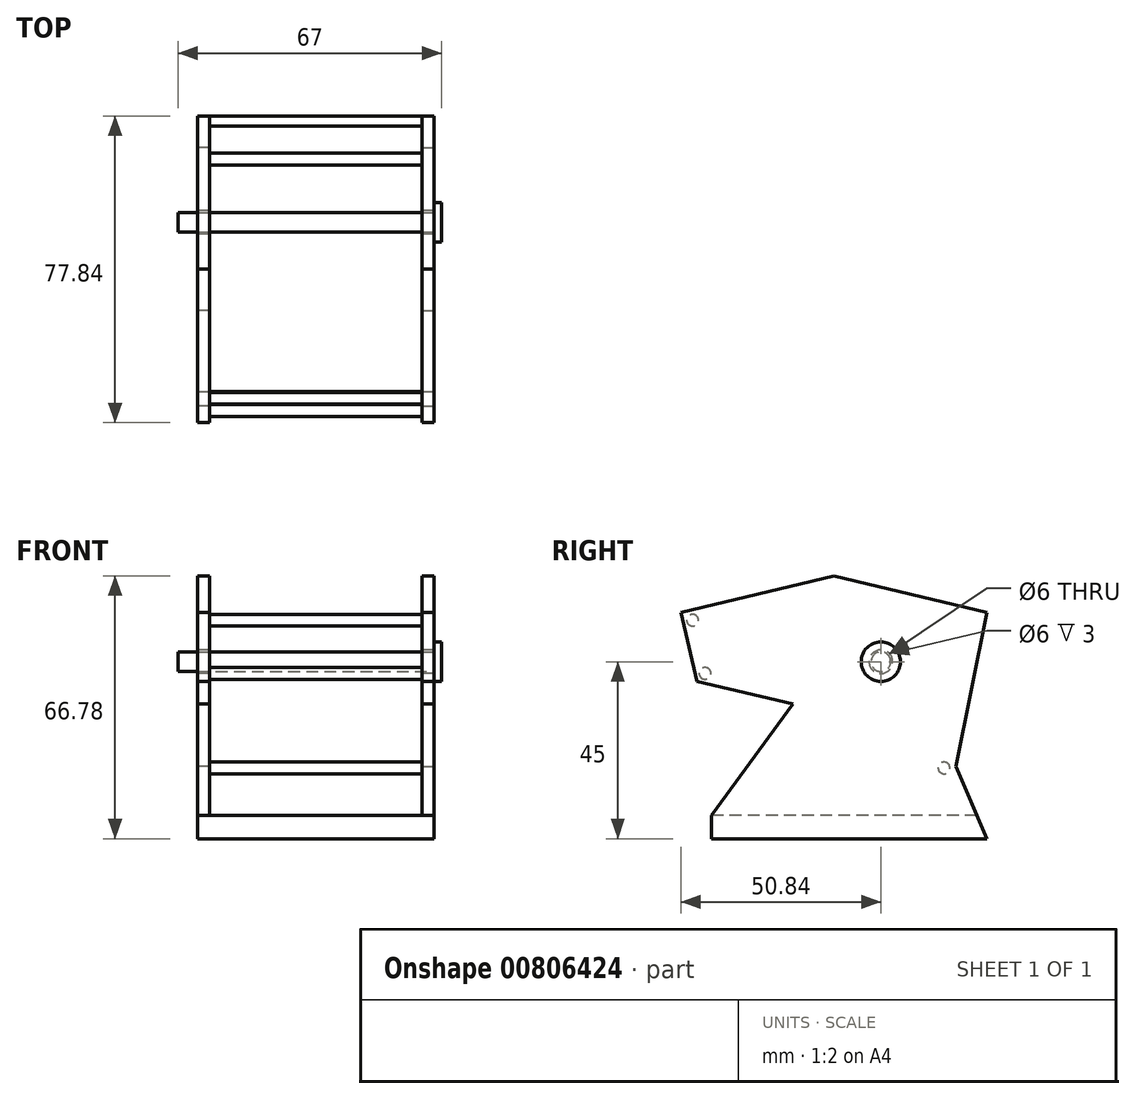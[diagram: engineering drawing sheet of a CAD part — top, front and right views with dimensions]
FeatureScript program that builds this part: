
annotation { "Feature Type Name" : "Feature", "Feature Type Description" : "" }
export const myFeature = defineFeature(function(context is Context, id is Id, definition is map)
    precondition{}
    {
        {
            var Q0;
            Q0=qCreatedBy(makeId("Right.planeOp"),FACE);
            var sketch = newSketch(context, id + "F0", { "sketchPlane" : qUnion([Q0])});
            skLineSegment(sketch, "E0", {"start": v(-35, 0) * mm, "end": v(35, 0) * mm});
            skLineSegment(sketch, "E1", {"start": v(35, 0) * mm, "end": v(27.05, 18.35) * mm});
            skLineSegment(sketch, "E2", {"start": v(27.05, 18.35) * mm, "end": v(35, 57.55) * mm});
            skLineSegment(sketch, "E3", {"start": v(35, 57.55) * mm, "end": v(-3.92, 66.78) * mm});
            skLineSegment(sketch, "E4", {"start": v(-3.92, 66.78) * mm, "end": v(-42.84, 57.55) * mm});
            skLineSegment(sketch, "E5", {"start": v(-42.84, 57.55) * mm, "end": v(-38.69, 40.04) * mm});
            skLineSegment(sketch, "E6", {"start": v(-38.69, 40.04) * mm, "end": v(-14.36, 34.27) * mm});
            skLineSegment(sketch, "E7", {"start": v(-14.36, 34.27) * mm, "end": v(-35, 6) * mm});
            skLineSegment(sketch, "E8", {"start": v(-35, 6) * mm, "end": v(-35, 0) * mm});
            skLineSegment(sketch, "E9", {"start": v(-35, 6) * mm, "end": v(32.4, 6) * mm});
            skSolve(sketch);
        }
        {
            var Q0;
            {var subQ0=sQuery(id+"F0.wireOp",EDGE,"E0");Q0=makeQuery(id+"F0.imprint","IMPRINT",FACE,{"disambiguationData":[TD([[makeQuery(id+"F0.imprint","IMPRINT",EDGE,{"derivedFrom":subQ0}),1.0]])]});}
            extrude(context, id + "F1", {"entities" : qUnion([Q0]), "oppositeDirection" : true, "depth" : 60 * mm, "offsetDistance" : 25 * mm});
        }
        {
            var Q0;
            {var subQ0=sQuery(id+"F0.wireOp",EDGE,"E2");Q0=makeQuery(id+"F0.imprint","IMPRINT",FACE,{"disambiguationData":[TD([[makeQuery(id+"F0.imprint","IMPRINT",EDGE,{"derivedFrom":subQ0}),1.0]])]});}
            extrude(context, id + "F2", {"entities" : qUnion([Q0]), "operationType" : NewBodyOperationType.ADD, "oppositeDirection" : true, "depth" : 3 * mm, "offsetDistance" : 25 * mm});
        }
        {
            var Q0;
            Q0=qCreatedBy(makeId("Right.planeOp"),FACE);
            cPlane(context, id + "F3", {"entities" : qUnion([Q0]), "cplaneType" : CPlaneType.OFFSET, "offset" : 60 * mm, "oppositeDirection" : true, "width" : 150 * mm, "height" : 150 * mm});
        }
        {
            var Q0;
            Q0=qCreatedBy(id+"F3.planeOp",FACE);
            var sketch = newSketch(context, id + "F4", { "sketchPlane" : qUnion([Q0])});
            skLineSegment(sketch, "E10.0.0", {"start": v(-14.36, 34.27) * mm, "end": v(-38.69, 40.04) * mm});
            skLineSegment(sketch, "E10.0.1", {"start": v(-38.69, 40.04) * mm, "end": v(-42.84, 57.55) * mm});
            skLineSegment(sketch, "E10.0.2", {"start": v(-42.84, 57.55) * mm, "end": v(-3.92, 66.78) * mm});
            skLineSegment(sketch, "E10.0.3", {"start": v(-3.92, 66.78) * mm, "end": v(35, 57.55) * mm});
            skLineSegment(sketch, "E10.0.4", {"start": v(35, 57.55) * mm, "end": v(27.05, 18.35) * mm});
            skLineSegment(sketch, "E10.0.5", {"start": v(27.05, 18.35) * mm, "end": v(32.4, 6) * mm});
            skLineSegment(sketch, "E10.0.6", {"start": v(32.4, 6) * mm, "end": v(-35, 6) * mm});
            skLineSegment(sketch, "E10.0.7", {"start": v(-35, 6) * mm, "end": v(-14.36, 34.27) * mm});
            skCircle(sketch, "E11", {"center": v(8, 45) * mm, "radius": 25 * mm, "construction": true});
            skCircle(sketch, "E12", {"center": v(8, 45) * mm, "radius": 3 * mm});
            skSolve(sketch);
        }
        {
            var Q0;
            Q0=makeQuery(id+"F4.imprint","IMPRINT",FACE,{"disambiguationData":[TD([[makeQuery(id+"F4.imprint","IMPRINT",EDGE,{"derivedFrom":sQuery(id+"F4.wireOp",EDGE,"E10.0.0")}),-1.0]])]});
            extrude(context, id + "F5", {"entities" : qUnion([Q0]), "operationType" : NewBodyOperationType.ADD, "depth" : 3 * mm, "offsetDistance" : 25 * mm});
        }
        {
            var Q0;
            Q0=makeQuery(id+"F4.imprint","IMPRINT",FACE,{"disambiguationData":[TD([[makeQuery(id+"F4.imprint","IMPRINT",EDGE,{"derivedFrom":sQuery(id+"F4.wireOp",EDGE,"E12")}),1.0]])]});
            extrude(context, id + "F6", {"entities" : qUnion([Q0]), "operationType" : NewBodyOperationType.REMOVE, "depth" : 60 * mm, "offsetDistance" : 25 * mm});
        }
        {
            var Q0;
            Q0=qCreatedBy(makeId("Right.planeOp"),FACE);
            var sketch = newSketch(context, id + "F7", { "sketchPlane" : qUnion([Q0])});
            skCircle(sketch, "E13", {"center": v(-39.84, 55.55) * mm, "radius": 1.5 * mm});
            skCircle(sketch, "E14", {"center": v(-36.69, 42.04) * mm, "radius": 1.5 * mm});
            skSolve(sketch);
        }
        {
            var Q0;
            Q0=makeQuery(id+"F7.imprint","IMPRINT",FACE,{"disambiguationData":[TD([[makeQuery(id+"F7.imprint","IMPRINT",EDGE,{"derivedFrom":sQuery(id+"F7.wireOp",EDGE,"E13")}),1.0]])]});
            var Q1;
            Q1=makeQuery(id+"F7.imprint","IMPRINT",FACE,{"disambiguationData":[TD([[makeQuery(id+"F7.imprint","IMPRINT",EDGE,{"derivedFrom":sQuery(id+"F7.wireOp",EDGE,"E14")}),1.0]])]});
            extrude(context, id + "F8", {"entities" : qUnion([Q0, Q1]), "operationType" : NewBodyOperationType.ADD, "oppositeDirection" : true, "depth" : 60 * mm, "offsetDistance" : 25 * mm});
        }
        {
            var Q0;
            Q0=qCreatedBy(makeId("Right.planeOp"),FACE);
            var sketch = newSketch(context, id + "F9", { "sketchPlane" : qUnion([Q0])});
            skCircle(sketch, "E15", {"center": v(24.05, 18) * mm, "radius": 1.5 * mm});
            skSolve(sketch);
        }
        {
            var Q0;
            Q0=makeQuery(id+"F9.imprint","IMPRINT",FACE,{"disambiguationData":[TD([[makeQuery(id+"F9.imprint","IMPRINT",EDGE,{"derivedFrom":sQuery(id+"F9.wireOp",EDGE,"E15")}),1.0]])]});
            extrude(context, id + "F10", {"entities" : qUnion([Q0]), "operationType" : NewBodyOperationType.ADD, "oppositeDirection" : true, "depth" : 60 * mm, "offsetDistance" : 25 * mm});
        }
        {
            var Q0;
            Q0=qCreatedBy(makeId("Right.planeOp"),FACE);
            var sketch = newSketch(context, id + "F11", { "sketchPlane" : qUnion([Q0])});
            skPoint(sketch, "E16.0", {"position": v(8, 45) * mm});
            skCircle(sketch, "E17", {"center": v(8, 45) * mm, "radius": 2.5 * mm});
            skCircle(sketch, "E18", {"center": v(8, 45) * mm, "radius": 5 * mm});
            skSolve(sketch);
        }
        {
            var Q0;
            Q0=makeQuery(id+"F11.imprint","IMPRINT",FACE,{"disambiguationData":[TD([[makeQuery(id+"F11.imprint","IMPRINT",EDGE,{"derivedFrom":sQuery(id+"F11.wireOp",EDGE,"E17")}),1.0]])]});
            var Q1;
            Q1=sQuery(id+"F11.wireOp",EDGE,"E17");
            extrude(context, id + "F12", {"entities" : qUnion([Q0]), "surfaceEntities" : qUnion([Q1]), "oppositeDirection" : true, "depth" : 65 * mm, "offsetDistance" : 25 * mm});
        }
        {
            var Q0;
            Q0=makeQuery(id+"F11.imprint","IMPRINT",FACE,{"disambiguationData":[TD([[makeQuery(id+"F11.imprint","IMPRINT",EDGE,{"derivedFrom":sQuery(id+"F11.wireOp",EDGE,"E17")}),-1.0]])]});
            var Q1;
            Q1=makeQuery(id+"F11.imprint","IMPRINT",FACE,{"disambiguationData":[TD([[makeQuery(id+"F11.imprint","IMPRINT",EDGE,{"derivedFrom":sQuery(id+"F11.wireOp",EDGE,"E17")}),1.0]])]});
            var Q2;
            Q2=sQuery(id+"F11.wireOp",EDGE,"E18");
            extrude(context, id + "F13", {"entities" : qUnion([Q0, Q1]), "operationType" : NewBodyOperationType.ADD, "surfaceEntities" : qUnion([Q2]), "depth" : 2 * mm, "offsetDistance" : 25 * mm});
        }
    });
